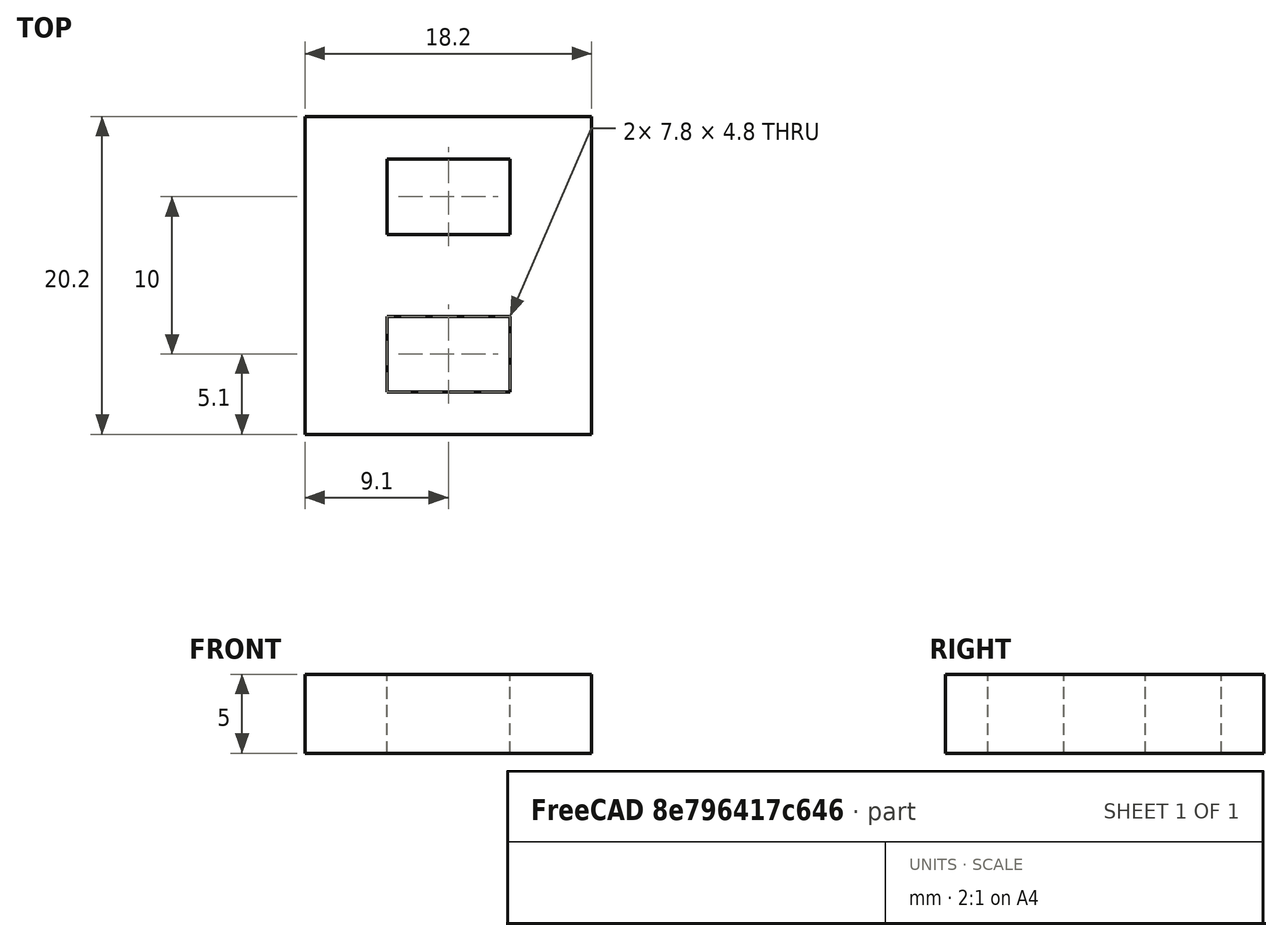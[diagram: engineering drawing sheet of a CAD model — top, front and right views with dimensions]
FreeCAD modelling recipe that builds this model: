
FCSTD DOCUMENT  (FreeCAD 0.16R6707 (Git))
Label: Assembler
License: All rights reserved
LicenseURL: http://en.wikipedia.org/wiki/All_rights_reserved
objects: Sketcher::SketchObject×1, PartDesign::Pad×1
note: 3 computed .brp shape members not serialized (recipe doc carries the construction recipe); baked Part::Feature solids carry a one-line shape summary decoded from their .brp

FEATURE [Sketcher::SketchObject] Sketch013
  Placement = pos=(0,-2.5,80) rot=(0,0,1;0rad)
  sketch-geometry (12):
    g0: LineSegment StartX=-9.1 StartY=10.1 StartZ=0 EndX=9.1 EndY=10.1 EndZ=0
    g1: LineSegment StartX=9.1 StartY=10.1 StartZ=0 EndX=9.1 EndY=-10.1 EndZ=0
    g2: LineSegment StartX=9.1 StartY=-10.1 StartZ=0 EndX=-9.1 EndY=-10.1 EndZ=0
    g3: LineSegment StartX=-9.1 StartY=-10.1 StartZ=0 EndX=-9.1 EndY=10.1 EndZ=0
    g4: LineSegment StartX=-3.9 StartY=7.4 StartZ=0 EndX=3.9 EndY=7.4 EndZ=0
    g5: LineSegment StartX=3.9 StartY=7.4 StartZ=0 EndX=3.9 EndY=2.6 EndZ=0
    g6: LineSegment StartX=3.9 StartY=2.6 StartZ=0 EndX=-3.9 EndY=2.6 EndZ=0
    g7: LineSegment StartX=-3.9 StartY=2.6 StartZ=0 EndX=-3.9 EndY=7.4 EndZ=0
    g8: LineSegment StartX=-3.9 StartY=-2.6 StartZ=0 EndX=3.9 EndY=-2.6 EndZ=0
    g9: LineSegment StartX=3.9 StartY=-2.6 StartZ=0 EndX=3.9 EndY=-7.4 EndZ=0
    g10: LineSegment StartX=3.9 StartY=-7.4 StartZ=0 EndX=-3.9 EndY=-7.4 EndZ=0
    g11: LineSegment StartX=-3.9 StartY=-7.4 StartZ=0 EndX=-3.9 EndY=-2.6 EndZ=0
  constraints (35):
    c: Coincident(g0,g1)
    c: Coincident(g1,g2)
    c: Coincident(g2,g3)
    c: Coincident(g3,g0)
    c: Horizontal(g0)
    c: Horizontal(g2)
    c: Vertical(g1)
    c: Vertical(g3)
    c: Symmetric(g0,g0,g-2)
    c: Symmetric(g1,g0,g-1)
    c: Coincident(g4,g5)
    c: Coincident(g5,g6)
    c: Coincident(g6,g7)
    c: Coincident(g7,g4)
    c: Horizontal(g4)
    c: Horizontal(g6)
    c: Vertical(g5)
    c: Vertical(g7)
    c: Coincident(g8,g9)
    c: Coincident(g9,g10)
    c: Coincident(g10,g11)
    c: Coincident(g11,g8)
    c: Horizontal(g8)
    c: Horizontal(g10)
    c: Vertical(g9)
    c: Vertical(g11)
    c: Symmetric(g8,g5,g-1)
    c: Symmetric(g4,g9,g-1)
    c: Symmetric(g5,g6,g-2)
    c: Symmetric(g8,g8,g-2)
    c: DistanceX(g0,g0) = 18.2
    c: DistanceX(g4,g4) = 7.8
    c: DistanceY(g1,g1) = 20.2
    c: DistanceY(g9,g9) = 4.8
    c: DistanceY(g8,g5) = 5.2
FEATURE [PartDesign::Pad] Pad013  label="TopAssembler_A"
  Length = 5
  Length2 = 100
  Placement = pos=(0,-2.5,80) rot=(0,0,1;0rad)
  Sketch = -> Sketch013
  Type = 0
